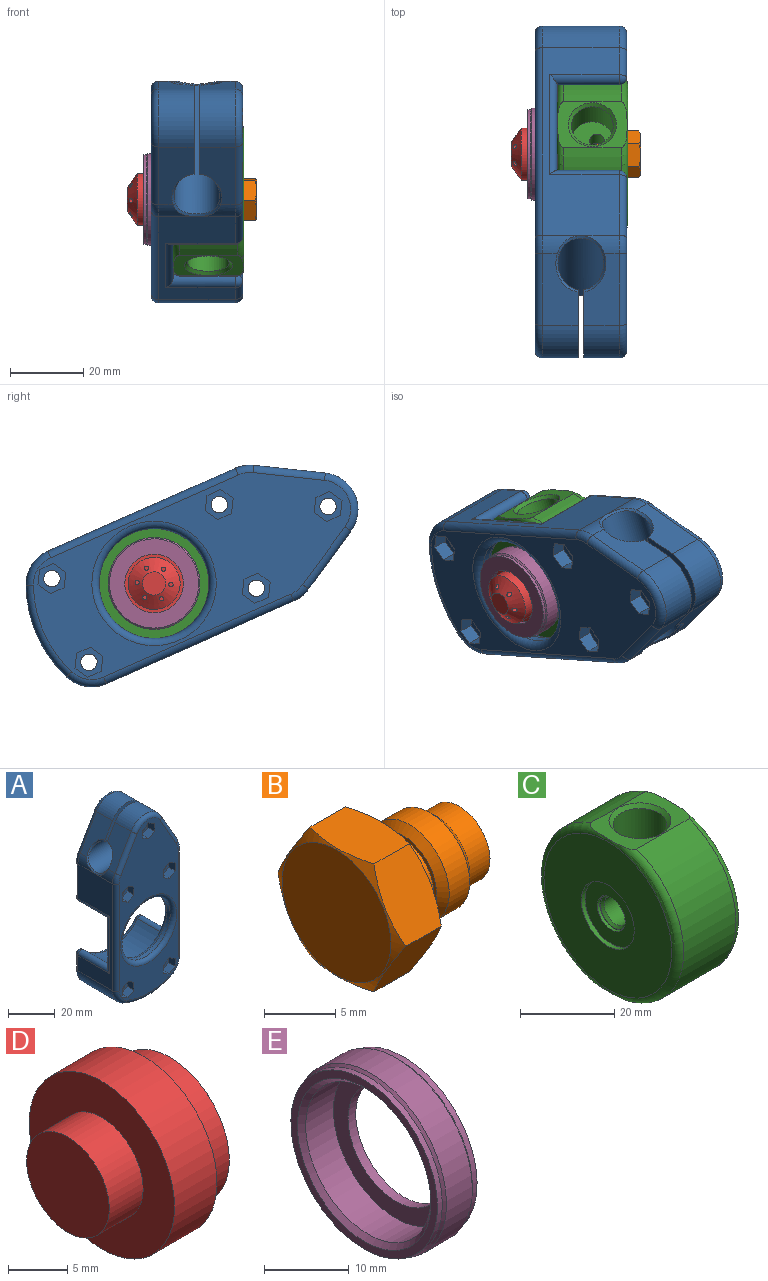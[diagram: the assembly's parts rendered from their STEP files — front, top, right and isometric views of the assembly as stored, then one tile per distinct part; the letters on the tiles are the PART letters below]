
ASSEMBLY  parts=5 mates=8
PART A: 111 faces, bbox 41.3x25x98.7 mm
  f0: plane 91x35.6mm, normal (0,-1,0), area 1730.6mm2, adj f24,f25,f26,f27,f28,f29,f31,f32
  f1: plane 43.04x35.6mm, normal (0,1,0), area 947.3mm2, adj f68,f70,f71,f72,f74,f75,f76,f77
  f2: plane 26.47x13.8mm, normal (0,1,0), area 241.6mm2, adj f4,f13,f61,f62,f63,f105,f110
  f3: plane 26.47x13.8mm, normal (0,-1,0), area 241.6mm2, adj f13,f22,f58,f59,f60,f107,f108
  f4: cylinder r=2.25mm len=7.75mm, axis (0,1,0), area 109.6mm2, adj f2,f51
  f5: cylinder r=2.25mm len=20.5mm, axis (0,1,0), area 289.8mm2, adj f44,f102
  f6: cylinder r=2.25mm len=20.5mm, axis (0,1,0), area 289.8mm2, adj f37,f103
  f7: cylinder r=2.25mm len=20.5mm, axis (0,1,0), area 289.8mm2, adj f30,f101
  f8: cylinder r=2.25mm len=20.5mm, axis (0,1,0), area 289.8mm2, adj f23,f100
  f9: plane 56.03x21mm, normal (1,0,0), area 608.1mm2, adj f18,f19,f65,f67,f68,f85,f91,f96
  f10: plane 56.03x21mm, normal (-1,0,0), area 608.1mm2, adj f20,f21,f64,f66,f75,f78,f92,f97
  f11: plane 35.6x18.04mm, normal (0,1,0), area 321.7mm2, adj f88,f91,f92,f93,f94,f95,f100,f101
  f12: cylinder r=15mm len=30mm, axis (0,-1,0), area 188.5mm2, adj f98,f99
  f13: cylinder r=6.25mm len=35.92mm, axis (-1,0,0), area 1239.7mm2, adj f2,f3,f105,f106,f107,f108,f109,f110
  f14: cylinder r=21.25mm len=32.54mm, axis (0,1,0), area 630mm2, adj f16,f18,f20,f88
  f15: cylinder r=21.25mm len=32.54mm, axis (0,1,0), area 630mm2, adj f16,f19,f21,f71
  f16: plane 42.5x35.6mm, normal (0,1,0), area 405.1mm2, adj f14,f15,f18,f19,f20,f21,f96,f97
  f17: cylinder r=35mm len=27.44mm, axis (0,1,0), area 592.1mm2, adj f66,f67,f81,f95
  f18: cylinder r=2mm len=19mm, axis (0,1,0), area 86.2mm2, adj f9,f14,f16,f89,f96
  f19: cylinder r=2mm len=19mm, axis (0,1,0), area 86.2mm2, adj f9,f15,f16,f69,f96
  f20: cylinder r=2mm len=19mm, axis (0,1,0), area 86.2mm2, adj f10,f14,f16,f90,f97
  f21: cylinder r=2mm len=19mm, axis (0,1,0), area 86.2mm2, adj f10,f15,f16,f73,f97
  f22: cylinder r=2.25mm len=11.25mm, axis (0,1,0), area 159mm2, adj f3,f104
  f23: plane 8.31x7.2mm, normal (0,-1,0), area 29mm2, adj f8,f24,f25,f26,f27,f28,f29
  f24: plane 4x3.6mm, normal (0.5,0,-0.87), area 16.6mm2, adj f0,f23,f25,f29
  f25: plane 4.16x4mm, normal (1,0,0), area 16.6mm2, adj f0,f23,f24,f26
  f26: plane 4x3.6mm, normal (0.5,0,0.87), area 16.6mm2, adj f0,f23,f25,f27
  f27: plane 4x3.6mm, normal (-0.5,0,0.87), area 16.6mm2, adj f0,f23,f26,f28
  f28: plane 4.16x4mm, normal (-1,0,0), area 16.6mm2, adj f0,f23,f27,f29
  f29: plane 4x3.6mm, normal (-0.5,0,-0.87), area 16.6mm2, adj f0,f23,f24,f28
  f30: plane 8.31x7.2mm, normal (0,-1,0), area 29mm2, adj f7,f31,f32,f33,f34,f35,f36
  f31: plane 4x3.6mm, normal (-0.5,0,0.87), area 16.6mm2, adj f0,f30,f32,f36
  f32: plane 4.16x4mm, normal (-1,0,0), area 16.6mm2, adj f0,f30,f31,f33
  f33: plane 4x3.6mm, normal (-0.5,0,-0.87), area 16.6mm2, adj f0,f30,f32,f34
  f34: plane 4x3.6mm, normal (0.5,0,-0.87), area 16.6mm2, adj f0,f30,f33,f35
  f35: plane 4.16x4mm, normal (1,0,0), area 16.6mm2, adj f0,f30,f34,f36
  f36: plane 4x3.6mm, normal (0.5,0,0.87), area 16.6mm2, adj f0,f30,f31,f35
  f37: plane 8.31x7.2mm, normal (0,-1,0), area 29mm2, adj f6,f38,f39,f40,f41,f42,f43
  f38: plane 4x3.6mm, normal (-0.5,0,0.87), area 16.6mm2, adj f0,f37,f39,f43
  f39: plane 4.16x4mm, normal (-1,0,0), area 16.6mm2, adj f0,f37,f38,f40
  f40: plane 4x3.6mm, normal (-0.5,0,-0.87), area 16.6mm2, adj f0,f37,f39,f41
  f41: plane 4x3.6mm, normal (0.5,0,-0.87), area 16.6mm2, adj f0,f37,f40,f42
  f42: plane 4.16x4mm, normal (1,0,0), area 16.6mm2, adj f0,f37,f41,f43
  f43: plane 4x3.6mm, normal (0.5,0,0.87), area 16.6mm2, adj f0,f37,f38,f42
  f44: plane 8.31x7.2mm, normal (0,-1,0), area 29mm2, adj f5,f45,f46,f47,f48,f49,f50
  f45: plane 4x3.6mm, normal (-0.5,0,0.87), area 16.6mm2, adj f0,f44,f46,f50
  f46: plane 4.16x4mm, normal (-1,0,0), area 16.6mm2, adj f0,f44,f45,f47
  f47: plane 4x3.6mm, normal (-0.5,0,-0.87), area 16.6mm2, adj f0,f44,f46,f48
  f48: plane 4x3.6mm, normal (0.5,0,-0.87), area 16.6mm2, adj f0,f44,f47,f49
  f49: plane 4.16x4mm, normal (1,0,0), area 16.6mm2, adj f0,f44,f48,f50
  f50: plane 4x3.6mm, normal (0.5,0,0.87), area 16.6mm2, adj f0,f44,f45,f49
  f51: plane 8.31x7.2mm, normal (0,-1,0), area 29mm2, adj f4,f52,f53,f54,f55,f56,f57
  f52: plane 4x3.6mm, normal (-0.5,0,0.87), area 16.6mm2, adj f0,f51,f53,f57
  f53: plane 4.16x4mm, normal (-1,0,0), area 16.6mm2, adj f0,f51,f52,f54
  f54: plane 4x3.6mm, normal (-0.5,0,-0.87), area 16.6mm2, adj f0,f51,f53,f55
  f55: plane 4x3.6mm, normal (0.5,0,-0.87), area 16.6mm2, adj f0,f51,f54,f56
  f56: plane 4.16x4mm, normal (1,0,0), area 16.6mm2, adj f0,f51,f55,f57
  f57: plane 4x3.6mm, normal (0.5,0,0.87), area 16.6mm2, adj f0,f51,f52,f56
  f58: plane 16.99x9.82mm, normal (0.87,0,0.5), area 139.1mm2, adj f3,f59,f65,f72,f108
  f59: cylinder r=10mm len=17.32mm, axis (0,-1,0), area 204.2mm2, adj f3,f58,f60,f74
  f60: plane 16.99x9.82mm, normal (-0.87,0,0.5), area 139.1mm2, adj f3,f59,f64,f76,f107
  f61: plane 16.99x9.82mm, normal (-0.87,0,0.5), area 139.1mm2, adj f2,f62,f64,f82,f105
  f62: cylinder r=10mm len=17.32mm, axis (0,-1,0), area 204.2mm2, adj f2,f61,f63,f84
  f63: plane 16.99x9.82mm, normal (0.87,0,0.5), area 139.1mm2, adj f2,f62,f65,f86,f110
  f64: cylinder r=10mm len=21mm, axis (0,1,0), area 61.6mm2, adj f10,f60,f61,f77,f80,f106
  f65: cylinder r=10mm len=21mm, axis (0,-1,0), area 61.6mm2, adj f9,f58,f63,f70,f87,f109
  f66: cylinder r=10mm len=21mm, axis (0,1,0), area 245.3mm2, adj f10,f17,f79,f94
  f67: cylinder r=10mm len=21mm, axis (0,1,0), area 245.3mm2, adj f9,f17,f83,f93
  f68: cylinder r=2mm len=18.07mm, axis (0,0,-1), area 56.8mm2, adj f1,f9,f69,f70
  f69: sphere r=2mm, area 6.2mm2, adj f19,f68,f71
  f70: torus R=8mm, axis (0,1,0), area 15.3mm2, adj f1,f65,f68,f72
  f71: torus R=23.25mm, axis (0,1,0), area 120.4mm2, adj f1,f15,f69,f73
  f72: cylinder r=2mm len=17.97mm, axis (-0.5,0,0.87), area 61.6mm2, adj f1,f58,f70,f74
  f73: sphere r=2mm, area 6.2mm2, adj f21,f71,f75
  f74: torus R=8mm, axis (0,1,0), area 61mm2, adj f1,f59,f72,f76
  f75: cylinder r=2mm len=18.07mm, axis (0,0,1), area 56.8mm2, adj f1,f10,f73,f77
  f76: cylinder r=2mm len=17.97mm, axis (-0.5,0,-0.87), area 61.6mm2, adj f1,f60,f74,f77
  f77: torus R=8mm, axis (0,1,0), area 15.3mm2, adj f1,f64,f75,f76
  f78: cylinder r=2mm len=56.03mm, axis (0,0,-1), area 176mm2, adj f0,f10,f79,f80
  f79: torus R=8mm, axis (0,-1,0), area 34mm2, adj f0,f66,f78,f81
  f80: torus R=8mm, axis (0,-1,0), area 15.3mm2, adj f0,f64,f78,f82
  f81: torus R=33mm, axis (0,-1,0), area 86.7mm2, adj f0,f17,f79,f83
  f82: cylinder r=2mm len=17.97mm, axis (-0.5,0,-0.87), area 61.6mm2, adj f0,f61,f80,f84
  f83: torus R=8mm, axis (0,-1,0), area 34mm2, adj f0,f67,f81,f85
  f84: torus R=8mm, axis (0,-1,0), area 61mm2, adj f0,f62,f82,f86
  f85: cylinder r=2mm len=56.03mm, axis (0,0,1), area 176mm2, adj f0,f9,f83,f87
  f86: cylinder r=2mm len=17.97mm, axis (-0.5,0,0.87), area 61.6mm2, adj f0,f63,f84,f87
  f87: torus R=8mm, axis (0,-1,0), area 15.3mm2, adj f0,f65,f85,f86
  f88: torus R=23.25mm, axis (0,1,0), area 120.4mm2, adj f11,f14,f89,f90
  f89: sphere r=2mm, area 7.5mm2, adj f18,f88,f91
  f90: sphere r=2mm, area 9.8mm2, adj f20,f88,f92
  f91: cylinder r=2mm len=8.04mm, axis (0,0,-1), area 25.3mm2, adj f9,f11,f89,f93
  f92: cylinder r=2mm len=8.04mm, axis (0,0,1), area 25.3mm2, adj f10,f11,f90,f94
  f93: torus R=8mm, axis (0,1,0), area 34mm2, adj f11,f67,f91,f95
  f94: torus R=8mm, axis (0,1,0), area 34mm2, adj f11,f66,f92,f95
  f95: torus R=33mm, axis (0,1,0), area 86.7mm2, adj f11,f17,f93,f94
  f96: cylinder r=2mm len=29.91mm, axis (0,0,1), area 87.7mm2, adj f9,f16,f18,f19
  f97: cylinder r=2mm len=29.91mm, axis (0,0,-1), area 87.7mm2, adj f10,f16,f20,f21
  f98: torus R=17mm, axis (0,1,0), area 310.4mm2, adj f12,f16
  f99: torus R=17mm, axis (0,-1,0), area 310.4mm2, adj f0,f12
  f100: cone r=2.25mm half-angle=45deg, axis (0,1,0), area 11.1mm2, adj f8,f11
  f101: cone r=2.25mm half-angle=45deg, axis (0,1,0), area 11.1mm2, adj f7,f11
  f102: cone r=2.25mm half-angle=45deg, axis (0,1,0), area 11.1mm2, adj f1,f5
  f103: cone r=2.25mm half-angle=45deg, axis (0,1,0), area 11.1mm2, adj f1,f6
  f104: cone r=2.25mm half-angle=45deg, axis (0,1,0), area 11.1mm2, adj f1,f22
  f105: bspline ~9.19x6.79mm, area 11.7mm2, adj f2,f13,f61,f106
  f106: bspline ~12.89x4.85mm, area 12.9mm2, adj f13,f64,f105,f107
  f107: bspline ~9.19x6.79mm, area 11.7mm2, adj f3,f13,f60,f106
  f108: bspline ~9.19x6.79mm, area 11.7mm2, adj f3,f13,f58,f109
  f109: bspline ~12.89x4.85mm, area 12.9mm2, adj f13,f65,f108,f110
  f110: bspline ~9.19x6.79mm, area 11.7mm2, adj f2,f13,f63,f109
PART B: 18 faces, bbox 12.2x12.7x12.7 mm
  f0: plane 5.5x4.49mm, normal (0,-0.87,0.5), area 26.3mm2, adj f1,f5,f8,f10
  f1: cone r=5.4mm half-angle=60deg, axis (-1,0,0), area 15.2mm2, adj f0,f2,f3,f8,f9,f10,f11
  f2: plane 6.35x4.48mm, normal (0,0,-1), area 26.3mm2, adj f1,f5,f8,f9
  f3: plane 5.5x4.49mm, normal (0,0.87,0.5), area 26.3mm2, adj f1,f5,f9,f10
  f4: plane 10.8x10.8mm, normal (-1,0,0), area 91.6mm2, adj f5
  f5: cone r=6.48mm half-angle=60deg, axis (1,0,0), area 15.2mm2, adj f0,f2,f3,f4,f8,f9,f10
  f6: plane 6.1x6.1mm, normal (1,0,0), area 29.2mm2, adj f7
  f7: cylinder r=3.05mm len=6.1mm, axis (1,0,0), area 44.1mm2, adj f6,f17
  f8: plane 5.5x4.49mm, normal (0,-0.87,-0.5), area 26.3mm2, adj f0,f1,f2,f5
  f9: plane 5.5x4.49mm, normal (0,0.87,-0.5), area 26.3mm2, adj f1,f2,f3,f5
  f10: plane 6.35x4.48mm, normal (0,0,1), area 26.3mm2, adj f0,f1,f3,f5
  f11: plane 10.8x10.8mm, normal (1,0,0), area 62.4mm2, adj f1,f12
  f12: cylinder r=3.05mm len=6.1mm, axis (1,0,0), area 38.3mm2, adj f11,f13
  f13: plane 6.68x6.68mm, normal (-1,0,0), area 5.8mm2, adj f12,f14
  f14: cone r=3.97mm half-angle=45deg, axis (1,0,0), area 20.5mm2, adj f13,f15
  f15: cylinder r=3.97mm len=7.94mm, axis (1,0,0), area 50.9mm2, adj f14,f16
  f16: cone r=3.34mm half-angle=45deg, axis (-1,0,0), area 20.5mm2, adj f15,f17
  f17: plane 6.68x6.68mm, normal (1,0,0), area 5.8mm2, adj f7,f16
PART C: 34 faces, bbox 25.3x45.4x45.4 mm
  f0: cylinder r=7.53mm len=15.06mm, axis (1,0,0), area 302.4mm2, adj f1,f26,f33
  f1: plane 17.63x17.63mm, normal (1,0,0), area 65.9mm2, adj f0,f2
  f2: cylinder r=8.81mm len=17.63mm, axis (1,0,0), area 244.8mm2, adj f1,f9
  f3: cylinder r=11.43mm len=22.86mm, axis (1,0,0), area 18.2mm2, adj f4,f25
  f4: plane 22.86x22.86mm, normal (1,0,0), area 22.5mm2, adj f3,f5
  f5: cylinder r=11.11mm len=22.23mm, axis (1,0,0), area 307.3mm2, adj f4,f6
  f6: cone r=10.36mm half-angle=45deg, axis (-1,0,0), area 72.1mm2, adj f5,f7
  f7: plane 20.71x20.71mm, normal (1,0,0), area 12.7mm2, adj f6,f8
  f8: cylinder r=10.16mm len=20.32mm, axis (1,0,0), area 40.5mm2, adj f7,f9
  f9: plane 20.32x20.32mm, normal (1,0,0), area 80.2mm2, adj f2,f8
  f10: plane 11.45x11.45mm, normal (0,0,1), area 89.9mm2, adj f11,f29
  f11: cylinder r=5.72mm len=11.45mm, axis (0,0,1), area 361.9mm2, adj f10,f12
  f12: cone r=6.58mm half-angle=45deg, axis (0,0,1), area 46.8mm2, adj f11,f14
  f13: cone r=5.72mm half-angle=45deg, axis (0,0,-1), area 46.8mm2, adj f20,f26
  f14: plane 19.07x13.69mm, normal (0,0,1), area 117.4mm2, adj f12,f21,f22,f23,f24
  f15: plane 8.38x8.38mm, normal (-1,0,0), area 5.7mm2, adj f19,f30
  f16: cylinder r=3.4mm len=12.13mm, axis (1,0,0), area 245.2mm2, adj f19,f29,f33
  f17: plane 15.88x15.88mm, normal (-1,0,0), area 6.3mm2, adj f18,f32
  f18: cylinder r=7.94mm len=15.88mm, axis (1,0,0), area 88.5mm2, adj f17,f27
  f19: cone r=3.4mm half-angle=45deg, axis (-1,0,0), area 18.7mm2, adj f15,f16
  f20: plane 19.07x13.69mm, normal (0,0,-1), area 117.6mm2, adj f13,f21,f22,f23,f24
  f21: torus R=19.17mm, axis (-1,0,0), area 310.3mm2, adj f14,f20,f22,f24,f27
  f22: cylinder r=20.95mm len=39.6mm, axis (1,0,0), area 816.6mm2, adj f14,f20,f21,f23
  f23: torus R=19.17mm, axis (-1,0,0), area 310.3mm2, adj f14,f20,f22,f24,f25
  f24: cylinder r=20.95mm len=39.6mm, axis (1,0,0), area 816.6mm2, adj f14,f20,f21,f23
  f25: plane 38.34x38.34mm, normal (1,0,0), area 744.3mm2, adj f3,f23
  f26: cylinder r=5.72mm len=14mm, axis (0,0,1), area 488.8mm2, adj f0,f13,f28,f33
  f27: plane 38.34x38.34mm, normal (-1,0,0), area 956.8mm2, adj f18,f21
  f28: plane 11.45x10.55mm, normal (0,0,-1), area 99.1mm2, adj f26,f33
  f29: cylinder r=2.03mm len=5.48mm, axis (0,0,1), area 70mm2, adj f10,f16
  f30: cylinder r=4.19mm len=8.38mm, axis (1,0,0), area 20.1mm2, adj f15,f31
  f31: plane 15.62x15.62mm, normal (-1,0,0), area 136.5mm2, adj f30,f32
  f32: cylinder r=7.81mm len=15.62mm, axis (1,0,0), area 37.4mm2, adj f17,f31
  f33: plane 15.06x14.4mm, normal (1,0,0), area 127.3mm2, adj f0,f16,f26,f28
PART D: 20 faces, bbox 15x17.4x17.4 mm
  f0: cylinder r=0.58mm len=5.34mm, axis (-1,0,0), area 18mm2, adj f1,f14
  f1: plane 1.15x1.15mm, normal (1,0,0), area 1mm2, adj f0
  f2: cylinder r=0.58mm len=5.4mm, axis (-1,0,0), area 18mm2, adj f3,f14
  f3: plane 1.15x1.15mm, normal (1,0,0), area 1mm2, adj f2
  f4: plane 1.15x1.15mm, normal (1,0,0), area 1mm2, adj f5
  f5: cylinder r=0.58mm len=5.39mm, axis (1,0,0), area 18mm2, adj f4,f14
  f6: cylinder r=0.58mm len=5.4mm, axis (1,0,0), area 18.1mm2, adj f14,f15
  f7: plane 9.91x9.91mm, normal (-1,0,0), area 77.1mm2, adj f8
  f8: cylinder r=4.95mm len=9.91mm, axis (1,0,0), area 126.5mm2, adj f7,f9
  f9: plane 17.42x17.42mm, normal (-1,0,0), area 161.4mm2, adj f8,f10
  f10: cylinder r=8.71mm len=17.42mm, axis (1,0,0), area 278.1mm2, adj f9,f11
  f11: plane 17.42x17.42mm, normal (1,0,0), area 79.6mm2, adj f10,f12
  f12: cylinder r=7.11mm len=14.22mm, axis (1,0,0), area 137.9mm2, adj f11,f14
  f13: plane 6.35x6.35mm, normal (1,0,0), area 31.7mm2, adj f14
  f14: cone r=3.17mm half-angle=55deg, axis (-1,0,0), area 148.9mm2, adj f0,f2,f5,f6,f12,f13,f16,f18
  f15: plane 1.15x1.15mm, normal (1,0,0), area 1mm2, adj f6
  f16: cylinder r=0.58mm len=5.32mm, axis (-1,0,0), area 17.9mm2, adj f14,f17
  f17: plane 1.15x1.15mm, normal (1,0,0), area 1mm2, adj f16
  f18: cylinder r=0.58mm len=5.4mm, axis (1,0,0), area 18mm2, adj f14,f19
  f19: plane 1.15x1.15mm, normal (1,0,0), area 1mm2, adj f18
PART E: 11 faces, bbox 6.6x25.1x25.1 mm
  f0: plane 24.4x24.4mm, normal (1,0,0), area 266.5mm2, adj f1,f10
  f1: cylinder r=8mm len=16mm, axis (1,0,0), area 65.3mm2, adj f0,f2
  f2: plane 20.85x20.85mm, normal (-1,0,0), area 140.4mm2, adj f1,f3
  f3: cylinder r=10.43mm len=20.85mm, axis (1,0,0), area 302.2mm2, adj f2,f4
  f4: cone r=10.43mm half-angle=45deg, axis (-1,0,0), area 65.7mm2, adj f3,f5
  f5: plane 24.4x24.4mm, normal (-1,0,0), area 79.6mm2, adj f4,f6
  f6: cylinder r=12.2mm len=24.4mm, axis (1,0,0), area 61.3mm2, adj f5,f7
  f7: cone r=12.2mm half-angle=45deg, axis (1,0,0), area 38.5mm2, adj f6,f8
  f8: cylinder r=12.55mm len=25.1mm, axis (1,0,0), area 339.1mm2, adj f7,f9
  f9: cone r=12.55mm half-angle=45deg, axis (-1,0,0), area 38.5mm2, adj f8,f10
  f10: cylinder r=12.2mm len=24.4mm, axis (1,0,0), area 61.3mm2, adj f0,f9
PLACE A rot(axis=(0.48,0.48,-0.74),107.3deg) t=(-6,27.62,-23.24)mm fixed
PLACE B rot(axis=(0,-1,-0.03),180deg) t=(9.65,-8.96,-7.06)mm
PLACE C rot(axis=(0,0.21,0.98),180deg) t=(9.65,-8.96,-7.06)mm
PLACE D rot(axis=(0,0.53,-0.85),180deg) t=(9.81,-8.96,-7.06)mm
PLACE E rot(axis=(0,-0.23,-0.97),180deg) t=(9.81,-8.96,-7.06)mm
MATE planar C.f0 <-> B.f1  axis (1,0,0) through (18.29,-8.96,-7.06)mm
MATE cylindrical B.f1 <-> C.f0  axis (-1,0,0) through (14.64,-8.96,-7.06)mm
MATE cylindrical C.f0 <-> D.f8  axis (-1,0,0) through (-3.84,-8.96,-7.06)mm
MATE parallel A.f9 <-> C.f11  axis (0,-0.4,-0.91) through (5.57,-25.84,-21.25)mm
MATE planar D.f8 <-> E.f1  axis (-1,0,0) through (-6.71,-8.96,-7.06)mm
MATE cylindrical C.f0 <-> A.f17  axis (-1,0,0) through (9.65,-8.96,-7.06)mm
MATE cylindrical E.f1 <-> D.f8  axis (-1,0,0) through (-4.71,-8.96,-7.06)mm
MATE planar C.f0 <-> D.f8  axis (-1,0,0) through (-1.63,-8.96,-7.06)mm
